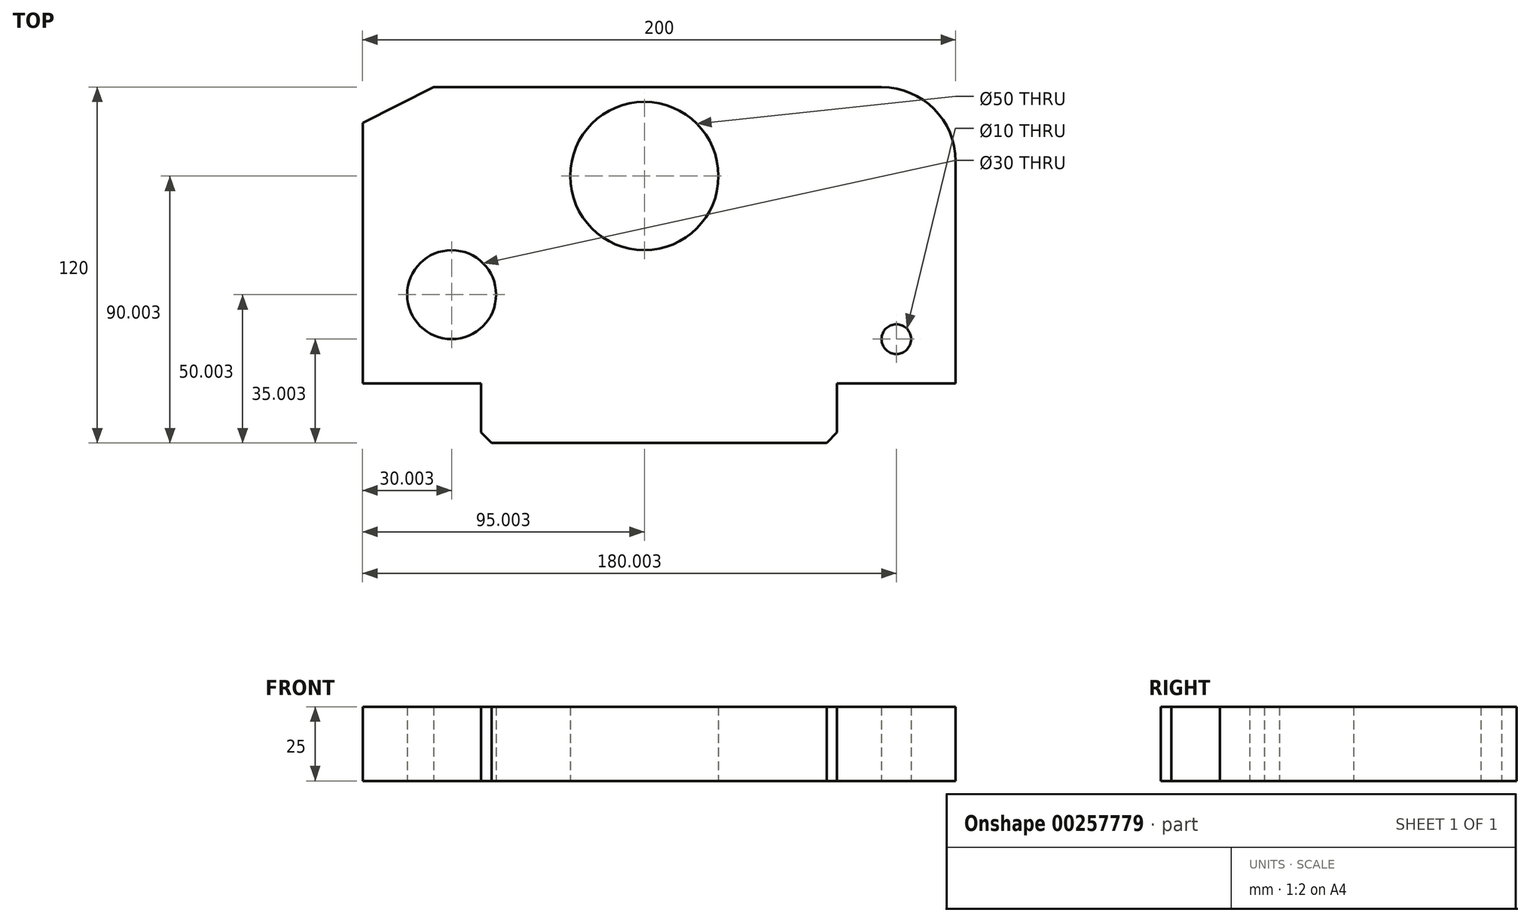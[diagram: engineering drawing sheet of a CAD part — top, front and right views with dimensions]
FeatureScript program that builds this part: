
annotation { "Feature Type Name" : "Feature", "Feature Type Description" : "" }
export const myFeature = defineFeature(function(context is Context, id is Id, definition is map)
    precondition{}
    {
        {
            var Q0;
            Q0=qCreatedBy(makeId("Top.planeOp"),FACE);
            var sketch = newSketch(context, id + "F0", { "sketchPlane" : qUnion([Q0])});
            skLineSegment(sketch, "E0", {"start": v(-53.82, 42.56) * mm, "end": v(-53.82, -45.44) * mm});
            skLineSegment(sketch, "E1", {"start": v(-53.82, 42.56) * mm, "end": v(-29.82, 54.56) * mm});
            skLineSegment(sketch, "E2", {"start": v(-29.82, 54.56) * mm, "end": v(121.18, 54.56) * mm});
            skLineSegment(sketch, "E3", {"start": v(146.18, 29.56) * mm, "end": v(146.18, -45.44) * mm});
            skPoint(sketch, "E4.visualSharp", {"position": v(146.18, 54.56) * mm});
            skArc(sketch, "E4.filletArc", {"start": v(146.18, 29.56) * mm, "mid": v(138.86, 47.24) * mm, "end": v(121.18, 54.56) * mm});
            skLineSegment(sketch, "E5", {"start": v(-53.82, -45.44) * mm, "end": v(-13.82, -45.44) * mm});
            skLineSegment(sketch, "E6", {"start": v(-13.82, -45.44) * mm, "end": v(-13.82, -61.9) * mm});
            skLineSegment(sketch, "E7", {"start": v(-10.28, -65.44) * mm, "end": v(-13.82, -61.9) * mm});
            skPoint(sketch, "E8.orphan", {"position": v(-13.82, -65.44) * mm});
            skLineSegment(sketch, "E9", {"start": v(146.18, -45.44) * mm, "end": v(106.18, -45.44) * mm});
            skLineSegment(sketch, "E10", {"start": v(106.18, -45.44) * mm, "end": v(106.18, -61.9) * mm});
            skLineSegment(sketch, "E11", {"start": v(-10.28, -65.44) * mm, "end": v(102.65, -65.44) * mm});
            skLineSegment(sketch, "E12", {"start": v(106.18, -61.9) * mm, "end": v(102.65, -65.44) * mm});
            skCircle(sketch, "E13", {"center": v(126.18, -30.44) * mm, "radius": 5 * mm});
            skLineSegment(sketch, "E14", {"start": v(-29.82, 54.56) * mm, "end": v(41.18, 54.56) * mm});
            skCircle(sketch, "E15", {"center": v(41.18, 24.56) * mm, "radius": 25 * mm});
            skCircle(sketch, "E16", {"center": v(-23.82, -15.44) * mm, "radius": 15 * mm});
            skSolve(sketch);
        }
        {
            var Q0;
            Q0 = qSketchRegion(id + "F0", true);
            extrude(context, id + "F1", {"entities" : qUnion([Q0]), "depth" : 25 * mm});
        }
    });
